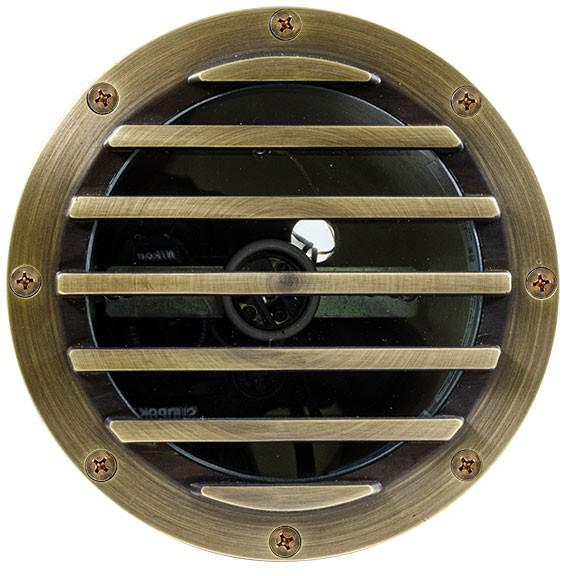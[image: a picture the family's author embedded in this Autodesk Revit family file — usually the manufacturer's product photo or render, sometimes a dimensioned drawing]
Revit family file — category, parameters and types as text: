
# Revit family: Alcon-9036-Revit-Family
name_source: partatom
category: Luminarias
units: mm (PartAtom-declared; Revit-internal decimal feet)

## family parameters
Anfitrión = Cara
Compartido = No
Corte con vacíos al cargar = No
Cota de conector redondo = Usar diámetro
Mantener orientación de anotación = No
Origen de luz = Sí
Punto de cálculo de habitación = No
Tipo de pieza = Normal

## types (1)
- Alcon-9036-Revit-Family
    Cambio de temperatura de color de luz atenuada = <Ninguno>
    Elevación por defecto = 4' - 0"
    Fabricante = Alcon Lighting
    Filtro de color = 16777215
    GLASS LENS = Analytical Panels
    HOUSING = <Por categoría>
    LENS GLASS = Glass
    Link to IES File = https://www.alconlighting.com
    Longitud de símbolo de origen de luz = 10' - 0"
    Modelo = Alcon Lighting 9036
    Product Data URL = https://www.alconlighting.com
    Product Page = https://www.alconlighting.com
    TAP LENS = <Por categoría>
    TOP FINISH = <Por categoría>
    URL = https://www.alconlighting.com
    Ángulo de campo de foco = 90.00°
    Ángulo de enfoque = 30.00°
    Ángulo de inclinación = 60.00°

## geometry (parser evidence)
native form markers: Sweep x3
no freeform markers — native parametric forms only
